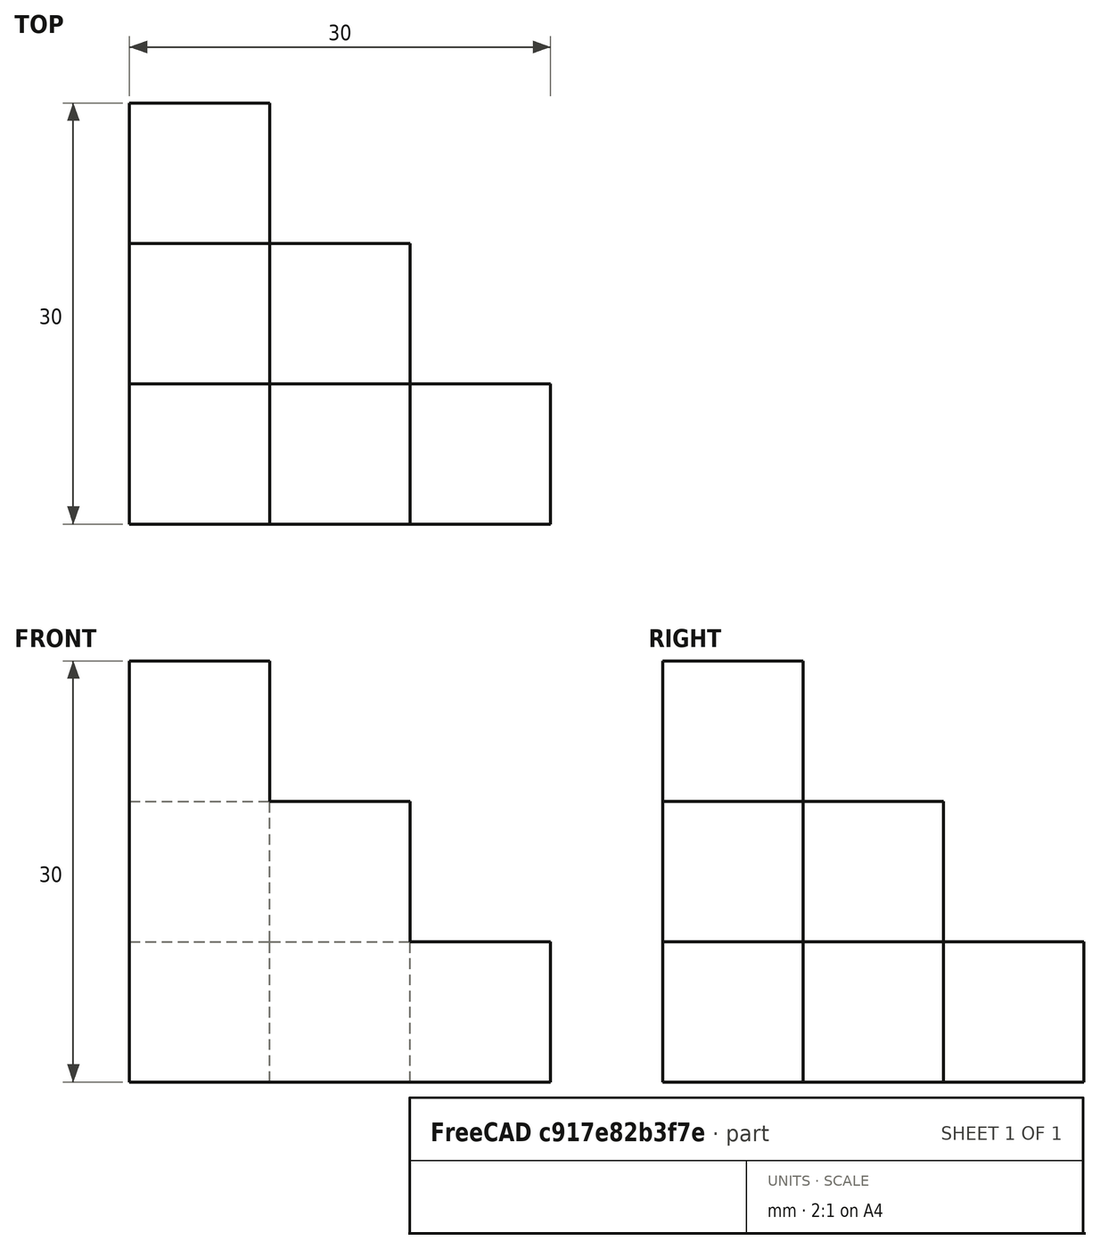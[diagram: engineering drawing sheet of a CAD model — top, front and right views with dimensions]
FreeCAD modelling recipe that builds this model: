
FCSTD DOCUMENT  (FreeCAD 0.21R33694 (Git))
Label: OJT1_T05R02_qubert_3
License: All rights reserved
LicenseURL: http://en.wikipedia.org/wiki/All_rights_reserved
objects: Part::Box×10, Part::MultiFuse×1
note: 11 computed .brp shape members not serialized (recipe doc carries the construction recipe); baked Part::Feature solids carry a one-line shape summary decoded from their .brp

FEATURE [Part::Box] Box  label="Cube"
  AttacherType = Attacher::AttachEngine3D
  Height = 10
  Length = 10
  Width = 10
FEATURE [Part::Box] Box001  label="Cube001"
  AttacherType = Attacher::AttachEngine3D
  Height = 10
  Length = 10
  Placement = pos=(10,0,0) rot=(0,0,1;0rad)
  Width = 10
FEATURE [Part::Box] Box002  label="Cube002"
  AttacherType = Attacher::AttachEngine3D
  Height = 10
  Length = 10
  Placement = pos=(0,10,0) rot=(0,0,1;0rad)
  Width = 10
FEATURE [Part::Box] Box003  label="Cube003"
  AttacherType = Attacher::AttachEngine3D
  Height = 10
  Length = 10
  Placement = pos=(20,0,0) rot=(0,0,1;0rad)
  Width = 10
FEATURE [Part::Box] Box004  label="Cube004"
  AttacherType = Attacher::AttachEngine3D
  Height = 10
  Length = 10
  Placement = pos=(0,20,0) rot=(0,0,1;0rad)
  Width = 10
FEATURE [Part::Box] Box005  label="Cube005"
  AttacherType = Attacher::AttachEngine3D
  Height = 10
  Length = 10
  Placement = pos=(10,10,0) rot=(0,0,1;0rad)
  Width = 10
FEATURE [Part::Box] Box006  label="Cube006"
  AttacherType = Attacher::AttachEngine3D
  Height = 10
  Length = 10
  Placement = pos=(0,0,10) rot=(0,0,1;0rad)
  Width = 10
FEATURE [Part::Box] Box007  label="Cube007"
  AttacherType = Attacher::AttachEngine3D
  Height = 10
  Length = 10
  Placement = pos=(10,0,10) rot=(0,0,1;0rad)
  Width = 10
FEATURE [Part::Box] Box008  label="Cube008"
  AttacherType = Attacher::AttachEngine3D
  Height = 10
  Length = 10
  Placement = pos=(0,10,10) rot=(0,0,1;0rad)
  Width = 10
FEATURE [Part::Box] Box009  label="Cube009"
  AttacherType = Attacher::AttachEngine3D
  Height = 10
  Length = 10
  Placement = pos=(0,0,20) rot=(0,0,1;0rad)
  Width = 10
FEATURE [Part::MultiFuse] Fusion
  Refine = true
  Shapes = -> [Box,Box001,Box002,Box003,Box004,Box005,Box006,Box007,Box008,Box009]
